FCSTD DOCUMENT  (FreeCAD 0.19R24366 (Git))
Label: Amplifier board hole drilling template
License: All rights reserved
LicenseURL: http://en.wikipedia.org/wiki/All_rights_reserved
objects: Sketcher::SketchObject×1, PartDesign::Body×1
note: 2 computed .brp shape members not serialized (recipe doc carries the construction recipe); baked Part::Feature solids carry a one-line shape summary decoded from their .brp

FEATURE [Sketcher::SketchObject] Sketch
  FullyConstrained = true
  MapMode = 5
  Support = -> [XY_Plane]
  sketch-geometry (33):
    g0: LineSegment StartX=-36.449 StartY=-43.71 StartZ=0 EndX=36.449 EndY=-43.71 EndZ=0
    g1: LineSegment StartX=-36.449 StartY=-43.71 StartZ=0 EndX=-36.449 EndY=38.84 EndZ=0
    g2: LineSegment StartX=36.449 StartY=-43.71 StartZ=0 EndX=36.449 EndY=38.84 EndZ=0
    g3: LineSegment StartX=-36.449 StartY=38.84 StartZ=0 EndX=-26.289 EndY=38.84 EndZ=0
    g4: LineSegment StartX=-26.289 StartY=38.84 StartZ=0 EndX=-26.289 EndY=49 EndZ=0
    g5: LineSegment StartX=-26.289 StartY=49 StartZ=0 EndX=26.289 EndY=49 EndZ=0
    g6: LineSegment StartX=26.289 StartY=49 StartZ=0 EndX=26.289 EndY=38.84 EndZ=0
    g7: LineSegment StartX=26.289 StartY=38.84 StartZ=0 EndX=36.449 EndY=38.84 EndZ=0
    g8: Circle CenterX=-30.353 CenterY=31.728 CenterZ=0 NormalX=0 NormalY=0 NormalZ=1 AngleXU=0 Radius=1.35
    g9: Circle CenterX=30.353 CenterY=31.728 CenterZ=0 NormalX=0 NormalY=0 NormalZ=1 AngleXU=0 Radius=1.35
    g10: Circle CenterX=-30.353 CenterY=-36.598 CenterZ=0 NormalX=0 NormalY=0 NormalZ=1 AngleXU=0 Radius=1.35
    g11: Circle CenterX=30.353 CenterY=-36.598 CenterZ=0 NormalX=0 NormalY=0 NormalZ=1 AngleXU=0 Radius=1.35
    g12: LineSegment StartX=-30.353 StartY=31.728 StartZ=0 EndX=-30.353 EndY=-36.598 EndZ=0
    g13: LineSegment StartX=-30.353 StartY=-36.598 StartZ=0 EndX=30.353 EndY=-36.598 EndZ=0
    g14: LineSegment StartX=30.353 StartY=-36.598 StartZ=0 EndX=30.353 EndY=31.728 EndZ=0
    g15: LineSegment StartX=-30.353 StartY=31.728 StartZ=0 EndX=30.353 EndY=31.728 EndZ=0
    g16: LineSegment StartX=-30.5 StartY=50 StartZ=0 EndX=-30.5 EndY=44.5 EndZ=0
    g17: LineSegment StartX=-30.5 StartY=44.5 StartZ=0 EndX=-36.5 EndY=44.5 EndZ=0
    g18: LineSegment StartX=-30.5 StartY=50 StartZ=0 EndX=30.5 EndY=50 EndZ=0
    g19: LineSegment StartX=30.5 StartY=50 StartZ=0 EndX=30.5 EndY=44.5 EndZ=0
    g20: LineSegment StartX=30.5 StartY=44.5 StartZ=0 EndX=36.5 EndY=44.5 EndZ=0
    g21: LineSegment StartX=36.5 StartY=44.5 StartZ=0 EndX=36.5 EndY=-44.5 EndZ=0
    g22: LineSegment StartX=36.5 StartY=-44.5 StartZ=0 EndX=30.5 EndY=-44.5 EndZ=0
    g23: LineSegment StartX=30.5 StartY=-44.5 StartZ=0 EndX=30.5 EndY=-50 EndZ=0
    g24: LineSegment StartX=30.5 StartY=-50 StartZ=0 EndX=-30.5 EndY=-50 EndZ=0
    g25: LineSegment StartX=-30.5 StartY=-50 StartZ=0 EndX=-30.5 EndY=-44.5 EndZ=0
    g26: LineSegment StartX=-30.5 StartY=-44.5 StartZ=0 EndX=-36.5 EndY=-44.5 EndZ=0
    g27: LineSegment StartX=-36.5 StartY=-44.5 StartZ=0 EndX=-36.5 EndY=44.5 EndZ=0
    g28: GeomPoint X=0 Y=50 Z=0
    g29: GeomPoint X=0 Y=-50 Z=0
    g30: LineSegment StartX=-36.449 StartY=-2.435 StartZ=0 EndX=-30.353 EndY=-2.435 EndZ=0
    g31: Circle CenterX=-22 CenterY=0 CenterZ=0 NormalX=0 NormalY=0 NormalZ=1 AngleXU=0 Radius=2.35
    g32: Circle CenterX=22 CenterY=0 CenterZ=0 NormalX=0 NormalY=0 NormalZ=1 AngleXU=0 Radius=2.35
  constraints (87):
    c: Coincident(g1,g0)
    c: Coincident(g2,g0)
    c: Vertical(g2)
    c: Coincident(g3,g1)
    c: Coincident(g4,g3)
    c: Vertical(g4)
    c: Coincident(g5,g4)
    c: Coincident(g6,g5)
    c: Coincident(g7,g6)
    c: Coincident(g7,g2)
    c: Horizontal(g7)
    c: Horizontal(g3)
    c: Symmetric(g4,g5,g-2)
    c: Symmetric(g3,g6,g-2)
    c: Symmetric(g0,g0,g-2)
    c: DistanceX(g0,g0) = 72.898
    c: Equal(g7,g4)
    c: DistanceX(g7,g7) = 10.16
    c: DistanceY(g2,g2) = 82.55
    c: Coincident(g12,g8)
    c: Coincident(g12,g10)
    c: Coincident(g13,g10)
    c: Coincident(g13,g11)
    c: Horizontal(g13)
    c: Coincident(g14,g11)
    c: Coincident(g14,g9)
    c: Coincident(g15,g8)
    c: Coincident(g15,g9)
    c: Vertical(g12)
    c: Symmetric(g8,g9,g-2)
    c: Equal(g8,g9)
    c: Equal(g9,g11)
    c: Equal(g11,g10)
    c: Diameter(g11) = 2.7
    c: DistanceX(g13,g13) = 60.706
    c: DistanceY(g14,g14) = 68.326
    c: Vertical(g16)
    c: Coincident(g17,g16)
    c: Horizontal(g17)
    c: Coincident(g18,g16)
    c: Coincident(g19,g18)
    c: Coincident(g20,g19)
    c: Horizontal(g20)
    c: Coincident(g21,g20)
    c: Vertical(g21)
    c: Coincident(g22,g21)
    c: Horizontal(g22)
    c: Coincident(g23,g22)
    c: Coincident(g24,g23)
    c: Coincident(g25,g24)
    c: Coincident(g26,g25)
    c: Coincident(g27,g26)
    c: Horizontal(g26)
    c: Vertical(g27)
    c: Vertical(g25)
    c: Vertical(g23)
    c: Coincident(g17,g27)
    c: Symmetric(g24,g23,g-2)
    c: Symmetric(g16,g18,g-2)
    c: Symmetric(g26,g21,g-2)
    c: DistanceY(g24,g16) = 100
    c: DistanceX(g26,g21) = 73
    c: Equal(g16,g25)
    c: DistanceY(g27,g27) = 89
    c: Symmetric(g16,g19,g-2)
    c: DistanceX(g24,g24) = 61
    c: DistanceY(g6,g18) = 1
    c: PointOnObject(g28,g-2)
    c: PointOnObject(g29,g-2)
    c: PointOnObject(g29,g24)
    c: PointOnObject(g28,g18)
    c: Equal(g1,g2)
    c: Horizontal(g30)
    c: Symmetric(g8,g10,g30)
    c: Symmetric(g1,g0,g30)
    c: Vertical(g14)
    c: Symmetric(g16,g24,g-1)
    c: PointOnObject(g31,g-1)
    c: Symmetric(g31,g32,g-2)
    c: Diameter(g31) = 4.7
    c: DistanceX(g31,g32) = 44
    c: Equal(g32,g31)
    c: DistanceY(g30,g31) = 2.435
    c: DistanceY(g30,g8) = 34.163
    c: DistanceY(g10,g30) = 34.163
    c: DistanceY(g30,g1) = 41.275
    c: DistanceY(g0,g30) = 41.275
FEATURE [PartDesign::Body] Body
  Group = -> [Sketch]
  Origin = -> Origin
